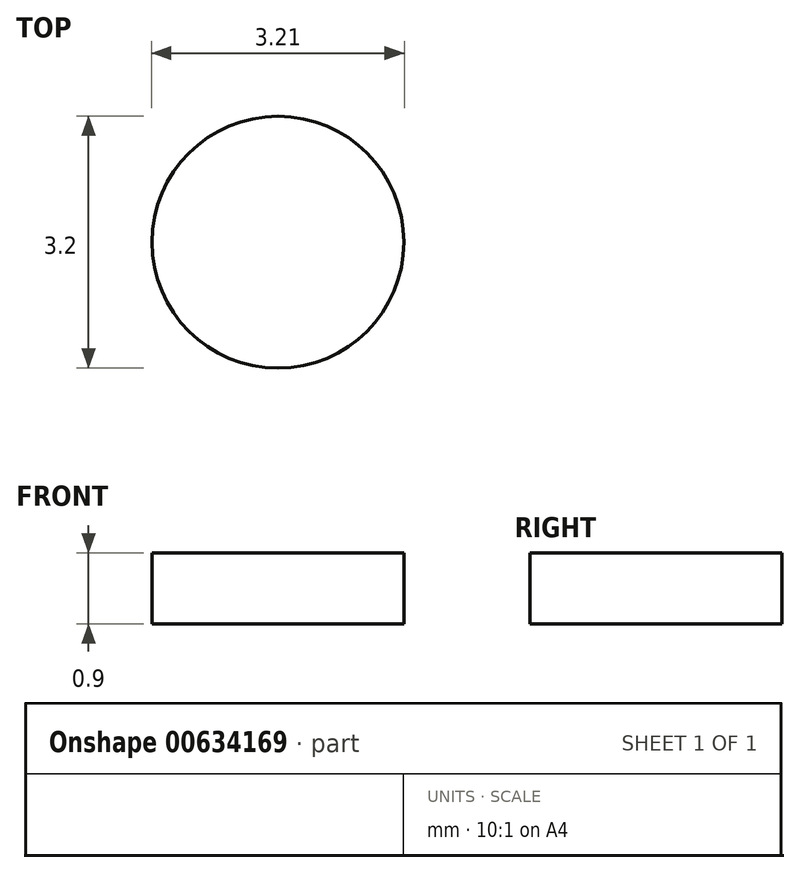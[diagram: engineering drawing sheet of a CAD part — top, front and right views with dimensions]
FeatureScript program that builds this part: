
annotation { "Feature Type Name" : "Feature", "Feature Type Description" : "" }
export const myFeature = defineFeature(function(context is Context, id is Id, definition is map)
    precondition{}
    {
        {
            var Q0;
            Q0=qCreatedBy(makeId("Top.planeOp"),FACE);
            var sketch = newSketch(context, id + "F0", { "sketchPlane" : qUnion([Q0])});
            skCircle(sketch, "E0", {"center": v(-15.22, -13.27) * mm, "radius": 1.6 * mm});
            skCircle(sketch, "E1", {"center": v(-4.57, 0.23) * mm, "radius": 1.6 * mm});
            skCircle(sketch, "E2", {"center": v(4.03, -13.27) * mm, "radius": 1.6 * mm});
            skCircle(sketch, "E3", {"center": v(17.12, -13.27) * mm, "radius": 1.6 * mm});
            skCircle(sketch, "E4", {"center": v(17.12, 0.03) * mm, "radius": 1.6 * mm});
            skCircle(sketch, "E5", {"center": v(17.12, 12.63) * mm, "radius": 1.6 * mm});
            skCircle(sketch, "E6", {"center": v(4.03, 12.63) * mm, "radius": 1.6 * mm});
            skLineSegment(sketch, "E7", {"start": v(-22.32, -15.77) * mm, "end": v(23.23, -15.77) * mm});
            skLineSegment(sketch, "E8", {"start": v(23.23, -15.77) * mm, "end": v(23.23, 14.77) * mm});
            skLineSegment(sketch, "E9", {"start": v(23.23, 14.77) * mm, "end": v(22.23, 15.77) * mm});
            skLineSegment(sketch, "E10", {"start": v(22.23, 15.77) * mm, "end": v(-3.78, 15.77) * mm});
            skLineSegment(sketch, "E11", {"start": v(-3.78, 15.77) * mm, "end": v(-11.32, 8.33) * mm});
            skLineSegment(sketch, "E12", {"start": v(-11.32, 8.33) * mm, "end": v(-16.16, 8.33) * mm});
            skLineSegment(sketch, "E13", {"start": v(-16.16, 8.33) * mm, "end": v(-17.67, 6.83) * mm});
            skLineSegment(sketch, "E14", {"start": v(-17.67, 6.83) * mm, "end": v(-17.67, 1.37) * mm});
            skLineSegment(sketch, "E15", {"start": v(-17.67, 1.37) * mm, "end": v(-22.23, 1.38) * mm});
            skLineSegment(sketch, "E16", {"start": v(-22.23, 1.38) * mm, "end": v(-23.22, 0.39) * mm});
            skLineSegment(sketch, "E17", {"start": v(-23.22, 0.39) * mm, "end": v(-23.22, -14.87) * mm});
            skLineSegment(sketch, "E18", {"start": v(-23.22, -14.87) * mm, "end": v(-22.32, -15.77) * mm});
            skLineSegment(sketch, "E19", {"start": v(-23.22, -7.33) * mm, "end": v(-23.22, -13.01) * mm});
            skLineSegment(sketch, "E20", {"start": v(-16.17, 8.33) * mm, "end": v(-11.32, 8.33) * mm});
            skCircle(sketch, "E21", {"center": v(-15.02, 5.63) * mm, "radius": 1.6 * mm});
            skSolve(sketch);
        }
        {
            var Q0;
            Q0=makeQuery(id+"F0.imprint","IMPRINT",FACE,{"disambiguationData":[TD([[makeQuery(id+"F0.imprint","IMPRINT",EDGE,{"derivedFrom":sQuery(id+"F0.wireOp",EDGE,"E0")}),1.0]])]});
            extrude(context, id + "F1", {"entities" : qUnion([Q0]), "depth" : 0.9 * mm, "offsetDistance" : 25 * mm});
        }
    });
